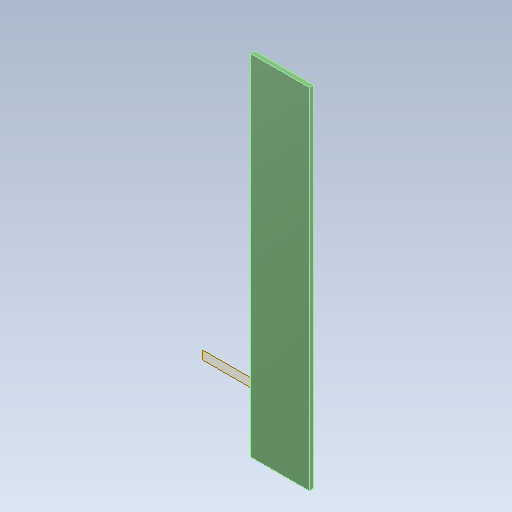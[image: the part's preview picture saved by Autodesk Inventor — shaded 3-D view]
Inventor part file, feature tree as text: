
AUTODESK INVENTOR PART (.ipt)
format: ipt  version: 2021 (Build 250183000, 183)  size: 85,504 bytes
history: native  units: in
note: dims shown in document units (in); Inventor stores cm internally (conversion verified against a paired STEP export)
features: other x2, plane x1, extrude x1, sketch x1
ambient origin geometry x8: Origin, YZ Plane, XZ Plane, XY Plane, X Axis, Y Axis, Z Axis, Center Point
bodies: Solid1 (feature_tree)
feature tree (5):
  plane  "Work Plane1"
  extrude  "Extrusion1"  Depth=5.3488in
  sketch  "Sketch1"  dims[d0=0.9in d1=5.3488in d2=0.064in d3=0.0in]
  other  "Tractive Light Assembly.iam"
  other  "Tractive Light Mount:1"
